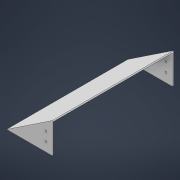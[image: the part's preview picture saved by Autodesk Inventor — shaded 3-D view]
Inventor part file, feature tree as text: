
AUTODESK INVENTOR PART (.ipt)
format: ipt  version: 2021 (Build 250183000, 183)  size: 134,144 bytes
history: native  units: mm
features: extrude x5, sketch x5
ambient origin geometry x8: Origin, YZ Plane, XZ Plane, XY Plane, X Axis, Y Axis, Z Axis, Center Point
bodies: Body1 (feature_tree)
feature tree (10):
  extrude  "Extrusion2"  Depth=75.0mm
  extrude  "Extrusion3"  Depth=25.0mm
  extrude  "Extrusion4"  Depth=200.0mm TaperAngle=0.0deg
  extrude  "Extrusion5"  Depth=2.0mm TaperAngle=0.0deg
  extrude  "Extrusion6"  Depth=2.0mm
  sketch  "Skizze1"  dims[d0=50.0mm d1=75.0mm]
  sketch  "Skizze2"  dims[d2=25.0mm d3=25.0mm]
  sketch  "Skizze3"  dims[d4=2.0mm d7=200.0mm d8=0.0mm]
  sketch  "Skizze4"  dims[d9=2.0mm d10=0.0mm d11=2.0mm d12=0.0mm]
  sketch  "Skizze5"  dims[d13=3.2mm d14=3.2mm d15=15.0mm d16=15.0mm d17=10.0mm d18=10.0mm d19=2.0mm d20=0.0mm d21=3.2mm d22=3.2mm d23=10.0mm d24=10.0mm d25=15.0mm d26=15.0mm d27=2.0mm d28=0.0mm]
